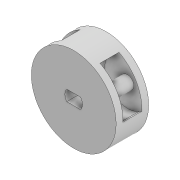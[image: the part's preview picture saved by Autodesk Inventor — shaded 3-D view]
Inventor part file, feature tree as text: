
AUTODESK INVENTOR PART (.ipt)
format: ipt  version: 2022.5 (Build 265521000, 521)  size: 208,384 bytes
history: native  units: mm
features: extrude x3, sketch x2, other x2, mirror x1, projected_geometry x1, reference x1
ambient origin geometry x8: Origin, YZ Plane, XZ Plane, XY Plane, X Axis, Y Axis, Z Axis, Center Point
bodies: Body1 (feature_tree)
feature tree (10):
  extrude  "Extrusion3"  Depth=9.5mm
  extrude  "Extrusion4"  Depth=2.0mm
  extrude  "Extrusion7"  Depth=2.0mm
  mirror  "Spiegeln1"
  sketch  "Skizze3"  dims[d10=25.0mm d11=9.5mm]
  projected_geometry  "Projizierte Kontur1"
  reference  "Referenz1"
  sketch  "Skizze9"  dims[d12=3.8mm d13=3.8mm d14=3.8mm d15=5.2mm d16=1.6mm d17=1.6mm d18=2.0mm d19=0.0mm d20=13.5mm d21=13.5mm d22=13.5mm d23=2.8mm d24=0.0mm d40=2.8mm d41=2.0mm d42=0.0mm d43=0.0mm]
  other  "Planktoscope_Mini_Peristalticpump_new.iam"
  other  "00_Bearing_4x13x5:1"
